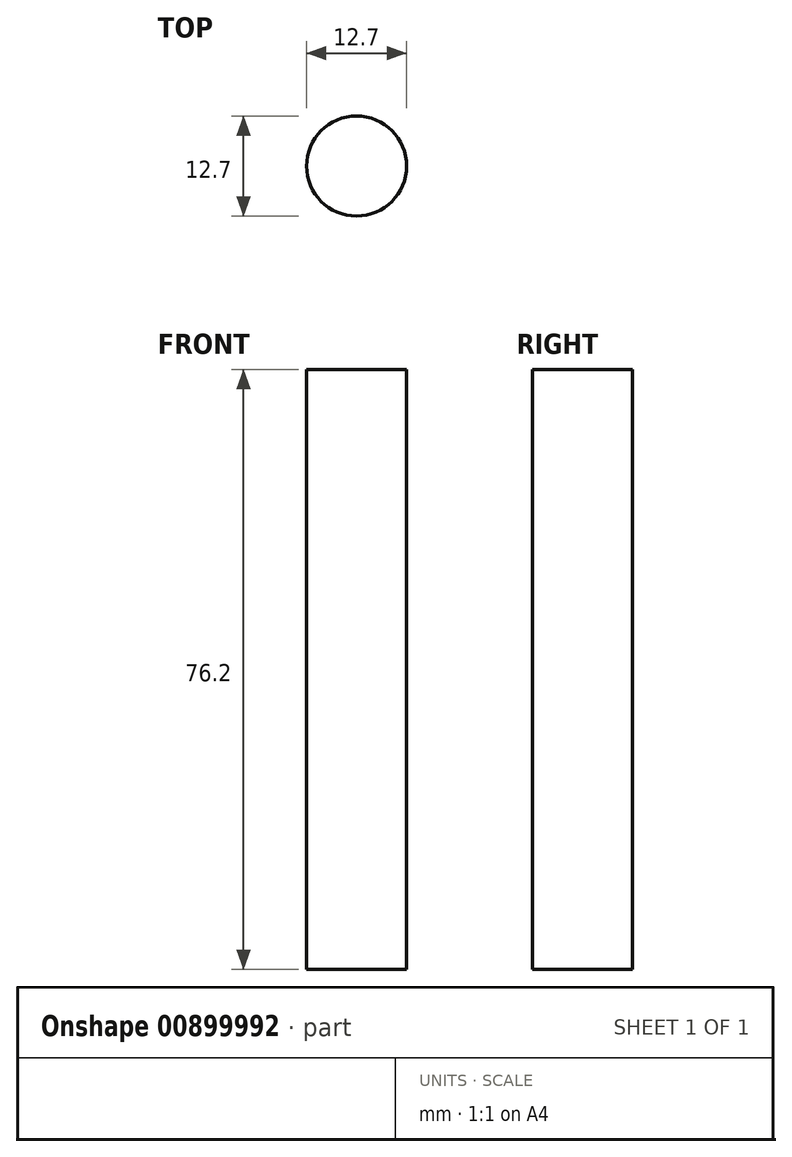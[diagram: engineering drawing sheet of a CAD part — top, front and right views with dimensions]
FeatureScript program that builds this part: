
annotation { "Feature Type Name" : "Feature", "Feature Type Description" : "" }
export const myFeature = defineFeature(function(context is Context, id is Id, definition is map)
    precondition{}
    {
        {
            var Q0;
            Q0=qCreatedBy(makeId("Top.planeOp"),FACE);
            var sketch = newSketch(context, id + "F0", { "sketchPlane" : qUnion([Q0])});
            skCircle(sketch, "E0", {"center": v(-42.9, -16.12) * mm, "radius": 6.35 * mm});
            skSolve(sketch);
        }
        {
            var Q0;
            Q0=makeQuery(id+"F0.imprint","IMPRINT",FACE,{"disambiguationData":[TD([[makeQuery(id+"F0.imprint","IMPRINT",EDGE,{"derivedFrom":sQuery(id+"F0.wireOp",EDGE,"E0")}),1.0]])]});
            extrude(context, id + "F1", {"entities" : qUnion([Q0]), "depth" : 76.2 * mm, "offsetDistance" : 25.4 * mm});
        }
    });
